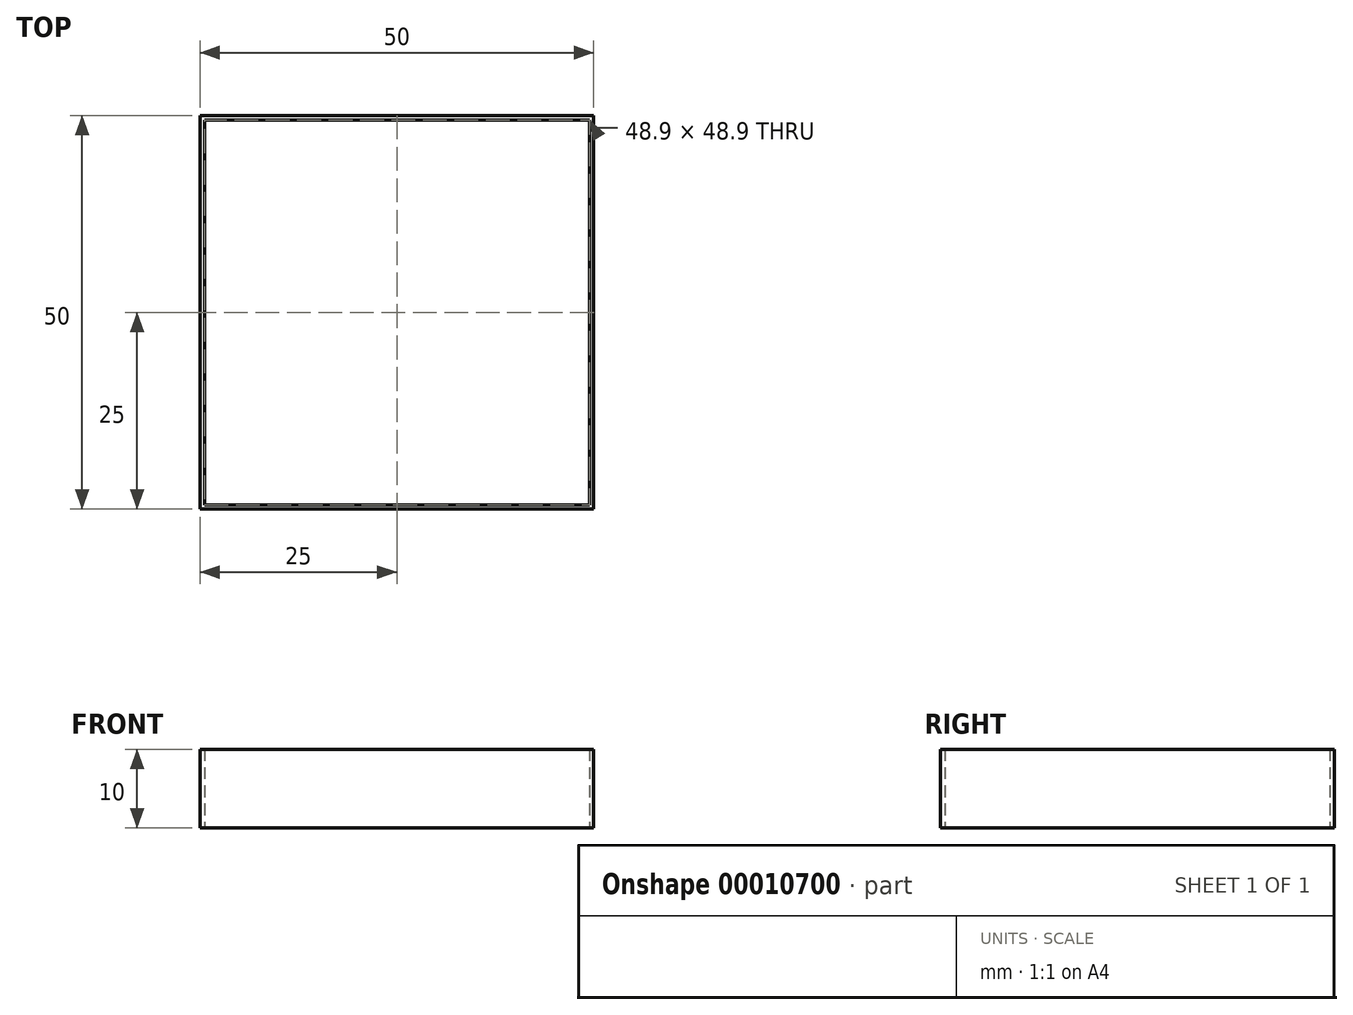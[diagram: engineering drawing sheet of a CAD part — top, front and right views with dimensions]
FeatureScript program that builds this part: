
annotation { "Feature Type Name" : "Feature", "Feature Type Description" : "" }
export const myFeature = defineFeature(function(context is Context, id is Id, definition is map)
    precondition{}
    {
        {
            var Q0;
            Q0=qCreatedBy(makeId("Top.planeOp"),FACE);
            var sketch = newSketch(context, id + "F1", { "sketchPlane" : qUnion([Q0])});
            skLineSegment(sketch, "E0.rect.bottom", {"start": v(24.45, 24.45) * mm, "end": v(-24.45, 24.45) * mm});
            skLineSegment(sketch, "E0.rect.top", {"start": v(24.45, -24.45) * mm, "end": v(-24.45, -24.45) * mm});
            skLineSegment(sketch, "E0.rect.left", {"start": v(24.45, 24.45) * mm, "end": v(24.45, -24.45) * mm});
            skLineSegment(sketch, "E0.rect.right", {"start": v(-24.45, 24.45) * mm, "end": v(-24.45, -24.45) * mm});
            skPoint(sketch, "E0.rect.middle", {"position": v(0, 0) * mm});
            skLineSegment(sketch, "E1.rect.bottom", {"start": v(25, 25) * mm, "end": v(-25, 25) * mm});
            skLineSegment(sketch, "E1.rect.top", {"start": v(25, -25) * mm, "end": v(-25, -25) * mm});
            skLineSegment(sketch, "E1.rect.left", {"start": v(25, 25) * mm, "end": v(25, -25) * mm});
            skLineSegment(sketch, "E1.rect.right", {"start": v(-25, 25) * mm, "end": v(-25, -25) * mm});
            skSolve(sketch);
        }
        {
            var Q0;
            Q0=makeQuery(id+"F1.imprint","IMPRINT",FACE,{"disambiguationData":[TD([[makeQuery(id+"F1.imprint","IMPRINT",EDGE,{"derivedFrom":sQuery(id+"F1.wireOp",EDGE,"E0.rect.bottom")}),-1.0]])]});
            extrude(context, id + "F0", {"entities" : qUnion([Q0]), "depth" : 10 * mm});
        }
    });
